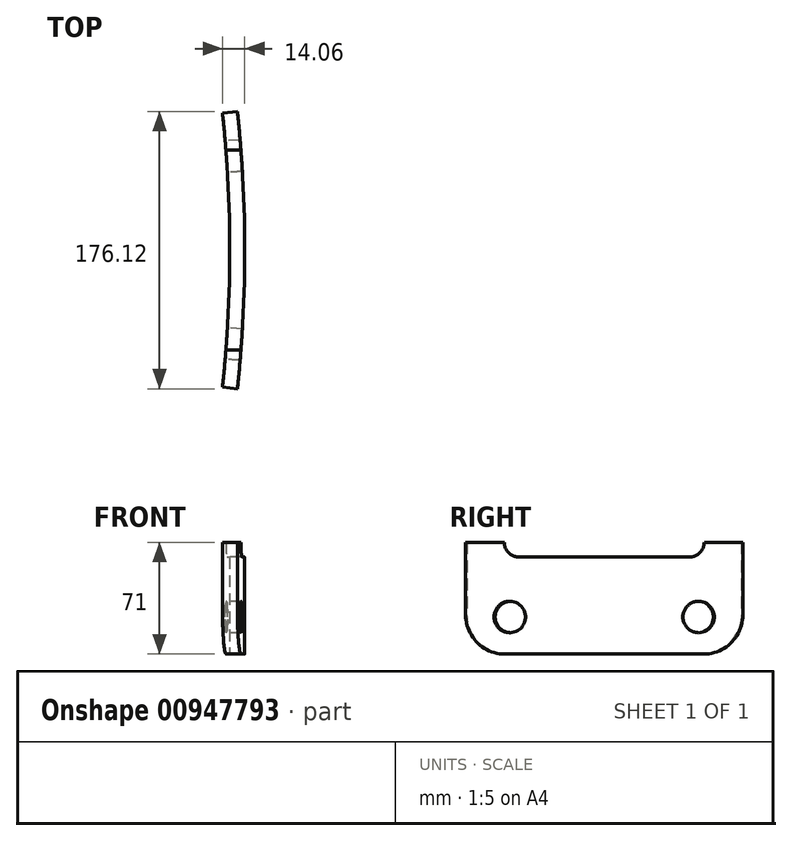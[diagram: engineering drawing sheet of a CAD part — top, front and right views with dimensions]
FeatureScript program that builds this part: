
annotation { "Feature Type Name" : "Feature", "Feature Type Description" : "" }
export const myFeature = defineFeature(function(context is Context, id is Id, definition is map)
    precondition{}
    {
        {
            var Q0;
            Q0=qCreatedBy(makeId("Top.planeOp"),FACE);
            var sketch = newSketch(context, id + "F0", { "sketchPlane" : qUnion([Q0])});
            skArc(sketch, "E0", {"start": v(835.47, 87.07) * mm, "mid": v(840, 0) * mm, "end": v(835.47, -87.07) * mm});
            skLineSegment(sketch, "E1", {"start": v(0, 0) * mm, "end": v(1155.94, 0) * mm, "construction": true});
            skLineSegment(sketch, "E2", {"start": v(835.47, 87.07) * mm, "end": v(844.95, 88.06) * mm});
            skLineSegment(sketch, "E3", {"start": v(835.47, -87.07) * mm, "end": v(844.95, -88.06) * mm});
            skArc(sketch, "E4", {"start": v(844.95, 88.06) * mm, "mid": v(849.52, 0) * mm, "end": v(844.95, -88.06) * mm});
            skSolve(sketch);
        }
        {
            var Q0;
            Q0 = qSketchRegion(id + "F0", true);
            extrude(context, id + "F1", {"entities" : qUnion([Q0]), "depth" : 71 * mm, "offsetDistance" : 25 * mm});
        }
        {
            var Q0;
            Q0=makeQuery(id+"F1.opExtrude","CAP_EDGE",EDGE,{"disambiguationData":[OSD([sQuery(id+"F0.wireOp",EDGE,"E3")])],"isStart":true});
            var Q1;
            Q1=makeQuery(id+"F1.opExtrude","CAP_EDGE",EDGE,{"disambiguationData":[OSD([sQuery(id+"F0.wireOp",EDGE,"E2")])],"isStart":true});
            fillet(context, id + "F2", {"entities" : qUnion([Q0, Q1]), "radius" : 25 * mm, "tangentPropagation" : true, "allowEdgeOverflow" : false});
        }
        {
            var Q0;
            Q0=qCreatedBy(makeId("Right.planeOp"),FACE);
            var sketch = newSketch(context, id + "F3", { "sketchPlane" : qUnion([Q0])});
            skPoint(sketch, "E5", {"position": v(0, 125.1) * mm});
            skLineSegment(sketch, "E6.bottom", {"start": v(53.95, 61.6) * mm, "end": v(-53.95, 61.6) * mm});
            skLineSegment(sketch, "E6.top", {"start": v(63.5, 188.6) * mm, "end": v(-63.5, 188.6) * mm});
            skLineSegment(sketch, "E6.left", {"start": v(63.5, 71.15) * mm, "end": v(63.5, 188.6) * mm});
            skLineSegment(sketch, "E6.right", {"start": v(-63.5, 71.15) * mm, "end": v(-63.5, 188.6) * mm});
            skPoint(sketch, "E7.visualSharp", {"position": v(63.5, 61.6) * mm});
            skArc(sketch, "E7.filletArc", {"start": v(53.95, 61.6) * mm, "mid": v(60.7, 64.4) * mm, "end": v(63.5, 71.15) * mm});
            skPoint(sketch, "E8.visualSharp", {"position": v(-63.5, 61.6) * mm});
            skArc(sketch, "E8.filletArc", {"start": v(-63.5, 71.15) * mm, "mid": v(-60.7, 64.4) * mm, "end": v(-53.95, 61.6) * mm});
            skSolve(sketch);
        }
        {
            var Q0;
            Q0 = qSketchRegion(id + "F3", true);
            extrude(context, id + "F4", {"entities" : qUnion([Q0]), "operationType" : NewBodyOperationType.REMOVE, "endBound" : BoundingType.THROUGH_ALL, "depth" : 25 * mm, "offsetDistance" : 25 * mm});
        }
        {
            var Q0;
            Q0=qCreatedBy(makeId("Right.planeOp"),FACE);
            var sketch = newSketch(context, id + "F5", { "sketchPlane" : qUnion([Q0])});
            skLineSegment(sketch, "E9", {"start": v(0, 0) * mm, "end": v(0, -32.91) * mm, "construction": true});
            skSolve(sketch);
        }
        {
            var Q0;
            Q0=qCreatedBy(makeId("Right.planeOp"),FACE);
            var Q1;
            Q1=sQuery(id+"F5.wireOp",EDGE,"E9");
            cPlane(context, id + "F6", {"entities" : qUnion([Q0, Q1]), "cplaneType" : CPlaneType.LINE_ANGLE, "offset" : 25 * mm, "angle" : 4.05 * degree, "width" : 150 * mm, "height" : 150 * mm});
        }
        {
            var Q0;
            Q0=qCreatedBy(makeId("Right.planeOp"),FACE);
            var Q1;
            Q1=sQuery(id+"F5.wireOp",EDGE,"E9");
            cPlane(context, id + "F7", {"entities" : qUnion([Q0, Q1]), "cplaneType" : CPlaneType.LINE_ANGLE, "offset" : 25 * mm, "angle" : 4.05 * degree, "oppositeDirection" : true, "width" : 150 * mm, "height" : 150 * mm});
        }
        {
            var Q0;
            Q0=qCreatedBy(id+"F6.planeOp",FACE);
            var sketch = newSketch(context, id + "F8", { "sketchPlane" : qUnion([Q0])});
            skLineSegment(sketch, "E10", {"start": v(-7.85, -2.43) * mm, "end": v(40.77, -2.43) * mm, "construction": true});
            skPoint(sketch, "E11", {"position": v(0, 23.57) * mm});
            skCircle(sketch, "E12", {"center": v(0, 23.57) * mm, "radius": 10 * mm});
            skSolve(sketch);
        }
        {
            var Q0;
            Q0 = qSketchRegion(id + "F8", true);
            extrude(context, id + "F9", {"entities" : qUnion([Q0]), "operationType" : NewBodyOperationType.REMOVE, "endBound" : BoundingType.THROUGH_ALL, "oppositeDirection" : true, "depth" : 25 * mm, "offsetDistance" : 25 * mm});
        }
        {
            var Q0;
            Q0=qCreatedBy(id+"F7.planeOp",FACE);
            var sketch = newSketch(context, id + "F10", { "sketchPlane" : qUnion([Q0])});
            skPoint(sketch, "E13", {"position": v(0, 0) * mm});
            skPoint(sketch, "E14", {"position": v(0, 23.57) * mm});
            skCircle(sketch, "E15", {"center": v(0, 23.57) * mm, "radius": 10 * mm});
            skLineSegment(sketch, "E16", {"start": v(31.7, -2.43) * mm, "end": v(-28.36, -2.43) * mm, "construction": true});
            skSolve(sketch);
        }
        {
            var Q0;
            Q0 = qSketchRegion(id + "F10", true);
            extrude(context, id + "F11", {"entities" : qUnion([Q0]), "operationType" : NewBodyOperationType.REMOVE, "endBound" : BoundingType.THROUGH_ALL, "oppositeDirection" : true, "depth" : 25 * mm, "offsetDistance" : 25 * mm});
        }
    });
